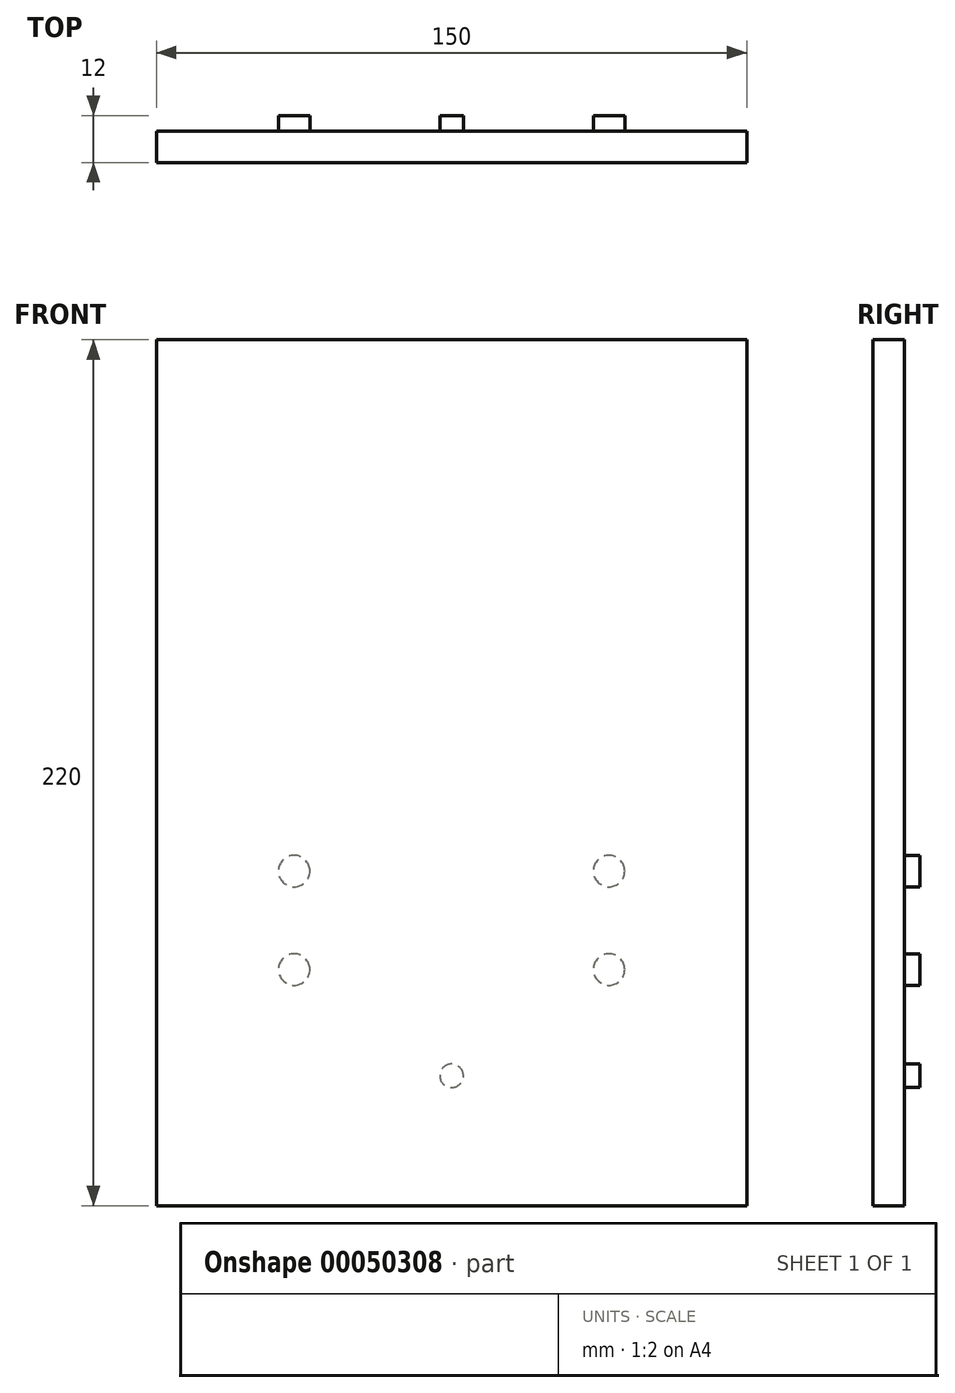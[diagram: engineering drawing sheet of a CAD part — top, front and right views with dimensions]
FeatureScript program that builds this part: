
annotation { "Feature Type Name" : "Feature", "Feature Type Description" : "" }
export const myFeature = defineFeature(function(context is Context, id is Id, definition is map)
    precondition{}
    {
        {
            var Q0;
            Q0=qCreatedBy(makeId("Front.planeOp"),FACE);
            var sketch = newSketch(context, id + "F0", { "sketchPlane" : qUnion([Q0])});
            skLineSegment(sketch, "E0.bottom", {"start": v(0, 0) * mm, "end": v(-150, 0) * mm});
            skLineSegment(sketch, "E0.top", {"start": v(0, -220) * mm, "end": v(-150, -220) * mm});
            skLineSegment(sketch, "E0.left", {"start": v(0, 0) * mm, "end": v(0, -220) * mm});
            skLineSegment(sketch, "E0.right", {"start": v(-150, 0) * mm, "end": v(-150, -220) * mm});
            skSolve(sketch);
        }
        {
            var Q0;
            Q0 = qSketchRegion(id + "F0", true);
            extrude(context, id + "F1", {"entities" : qUnion([Q0]), "depth" : 8 * mm});
        }
        {
            var Q0;
            Q0=makeQuery(id+"F1.opExtrude","CAP_FACE",FACE,{"disambiguationData":[OSD([sQuery(id+"F0.wireOp",EDGE,"E0.bottom"),sQuery(id+"F0.wireOp",EDGE,"E0.top"),sQuery(id+"F0.wireOp",EDGE,"E0.left"),sQuery(id+"F0.wireOp",EDGE,"E0.right")])],"isStart":false});
            var sketch = newSketch(context, id + "F2", { "sketchPlane" : qUnion([Q0])});
            skLineSegment(sketch, "E1", {"start": v(-75, 0) * mm, "end": v(-75, -220) * mm, "construction": true});
            skCircle(sketch, "E2", {"center": v(-75, -187) * mm, "radius": 3 * mm});
            skLineSegment(sketch, "E3", {"start": v(-115, 0) * mm, "end": v(-115, -220) * mm, "construction": true});
            skLineSegment(sketch, "E4", {"start": v(-35, 0) * mm, "end": v(-35, -220) * mm, "construction": true});
            skLineSegment(sketch, "E5", {"start": v(0, -135) * mm, "end": v(-150, -135) * mm, "construction": true});
            skLineSegment(sketch, "E6", {"start": v(0, -160) * mm, "end": v(-150, -160) * mm, "construction": true});
            skCircle(sketch, "E7", {"center": v(-35, -135) * mm, "radius": 4 * mm});
            skCircle(sketch, "E8", {"center": v(-35, -160) * mm, "radius": 4 * mm});
            skCircle(sketch, "E9", {"center": v(-115, -135) * mm, "radius": 4 * mm});
            skCircle(sketch, "E10", {"center": v(-115, -160) * mm, "radius": 4 * mm});
            skSolve(sketch);
        }
        {
            var Q0;
            Q0 = qSketchRegion(id + "F2", true);
            extrude(context, id + "F3", {"entities" : qUnion([Q0]), "operationType" : NewBodyOperationType.ADD, "oppositeDirection" : true, "depth" : 12 * mm});
        }
    });
